# Revit family: Hager-Vega_D-IP30-vacío-NoHosted-ES-es
name_source: partatom
category: Electrical Equipment
units: mm (PartAtom-declared; Revit-internal decimal feet)

## family parameters
Always vertical = Yes
Cut with Voids When Loaded = No
Panel Configuration = Two Columns, Circuits Across
Part Type = Panelboard
Room Calculation Point = No
Round Connector Dimension = Use Diameter
Shared = No
Work Plane-Based = Yes

## types (1)
- Montado empotrado IP30 A600 A537 P182 24 unidad de división - FU22AN
    Default Elevation = 1219 mm
    EF000003 - Tipo de montaje = EV000383 - Montado empotrado (escayola)
    EF000007 - Color = EV000202 - Blanco
    EF000008 - Anchura = 600 mm
    EF000040 - Altura = 537 mm  [stored 1.76181 ft]
    EF000049 - Profundidad = 182 mm  [stored 0.597113 ft]
    EF000116 - Número RAL = 9010
    EF000118 - Con placa de montaje = No
    EF000218 - Profundidad de instalación = 110 mm  [stored 0.360892 ft]
    EF000266 - Número de filas = 0
    EF000332 - Altura de la instalación = 537 mm  [stored 1.76181 ft]
    EF000339 - Tipo de cubierta = EV000494 - Ninguno
    EF000846 - Anchura de instalación = 600 mm
    EF001062 - Versión de EMC = No
    EF001088 - Posibilidad de extensión = Yes
    EF001131 - Profundidad interna = 110 mm  [stored 0.360892 ft]
    EF001134 - Carril DIN = Yes
    EF001596 - Material de la carcasa = EV000154 - Otros
    EF002950 - Anchura de unidades de división = 24
    EF005474 - Grado de protección (IP) = EV006410 - IP30
    EF006244 - Tapa/puerta transparente = No
    EF006306 - Con cierre = No
    EF009212 - Versión de la cubierta = EV009916 - Con muesca
    EF015776 - Borne de tierra = No
    EF015777 - Borne neutro = No
    EF015941 - Puerta de transmisión de señal = No
    HG000001 - Número de columnas = 0
    HG000002 - Con puerta o tapa = No
    HG000003 - Gama = Vega D
    HG000004 - Referencia del fabricante = FU22AN
    HG000005 - Grosor = 3 mm  [stored 0.00984252 ft]
    HG000006 - Empotrado = Yes
    HG000007 - Número de columnas vacías = 0
    HG000008 - Número de filas vacías = 0
    HG000009 - Puerta batiente doble = No
    HG000010 - Puertas asimétricas = No
    HG000011 - Filas vacías desde abajo = No
    HG000017 - Distancia entre polos = 18 mm  [stored 0.0590551 ft]
    Manufacturer = Hager
    Model = FU22AN
    Type Comments = Vega D

note: [stored X ft] marks values corroborated as IEEE doubles in the binary element streams (Revit-internal decimal feet)

## geometry (parser evidence)
native form markers: Sweep x12
no freeform markers — native parametric forms only
